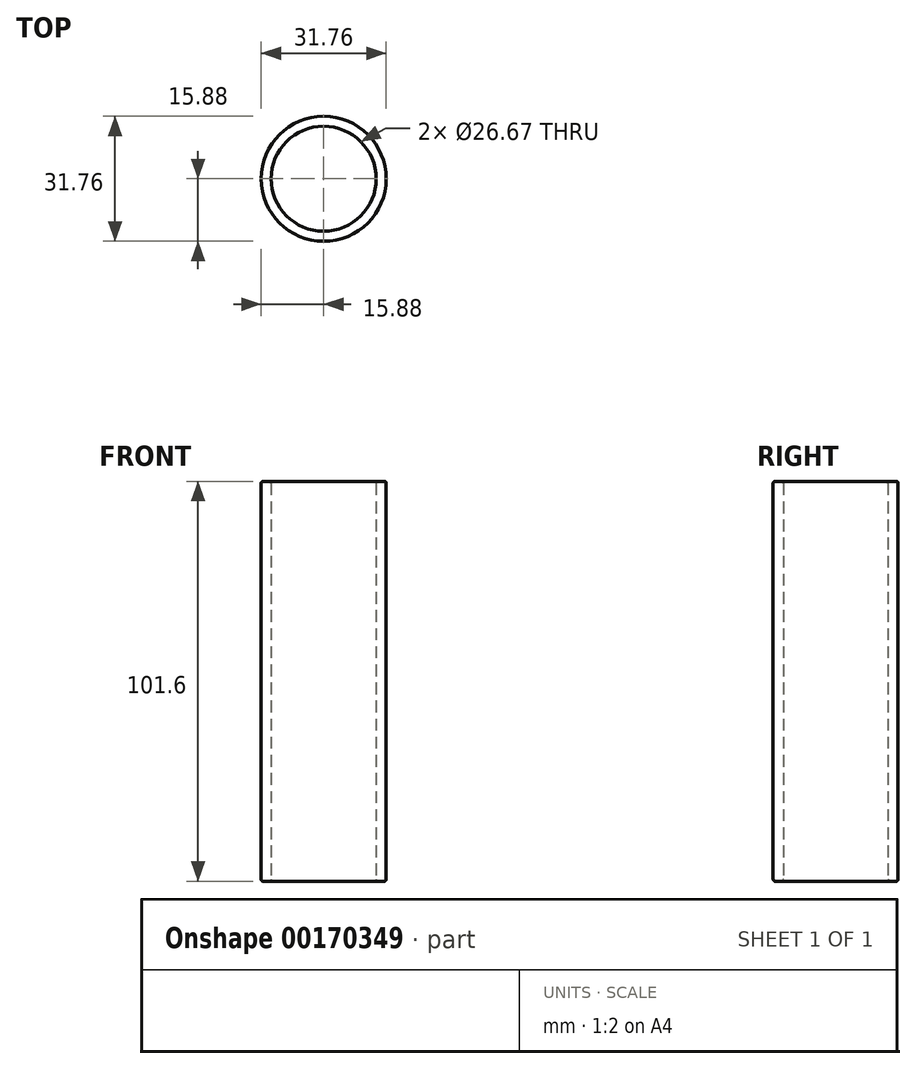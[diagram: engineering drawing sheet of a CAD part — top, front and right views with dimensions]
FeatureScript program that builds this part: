
annotation { "Feature Type Name" : "Feature", "Feature Type Description" : "" }
export const myFeature = defineFeature(function(context is Context, id is Id, definition is map)
    precondition{}
    {
        {
            var Q0;
            Q0=qCreatedBy(makeId("Top.planeOp"),FACE);
            var sketch = newSketch(context, id + "F0", { "sketchPlane" : qUnion([Q0])});
            skCircle(sketch, "E0", {"center": v(0, 0) * mm, "radius": 13.34 * mm});
            skCircle(sketch, "E1", {"center": v(0, 0) * mm, "radius": 15.88 * mm});
            skSolve(sketch);
        }
        {
            var Q0;
            Q0=makeQuery(id+"F0.imprint","IMPRINT",FACE,{"disambiguationData":[TD([[makeQuery(id+"F0.imprint","IMPRINT",EDGE,{"derivedFrom":sQuery(id+"F0.wireOp",EDGE,"E0")}),-1.0]])]});
            extrude(context, id + "F1", {"entities" : qUnion([Q0]), "endBound" : BoundingType.SYMMETRIC, "depth" : 101.6 * mm});
        }
        {
            var Q0;
            Q0=makeQuery(id+"F1.opExtrude","CAP_FACE",FACE,{"disambiguationData":[OSD([sQuery(id+"F0.wireOp",EDGE,"E0"),sQuery(id+"F0.wireOp",EDGE,"E1")])],"isStart":false});
            var Q1;
            Q1=makeQuery(id+"F1.opExtrude","CAP_FACE",FACE,{"disambiguationData":[OSD([sQuery(id+"F0.wireOp",EDGE,"E0"),sQuery(id+"F0.wireOp",EDGE,"E1")])],"isStart":true});
            fillet(context, id + "F2", {"entities" : qUnion([Q0, Q1]), "radius" : 0.5 * mm, "tangentPropagation" : true, "allowEdgeOverflow" : false});
        }
    });
